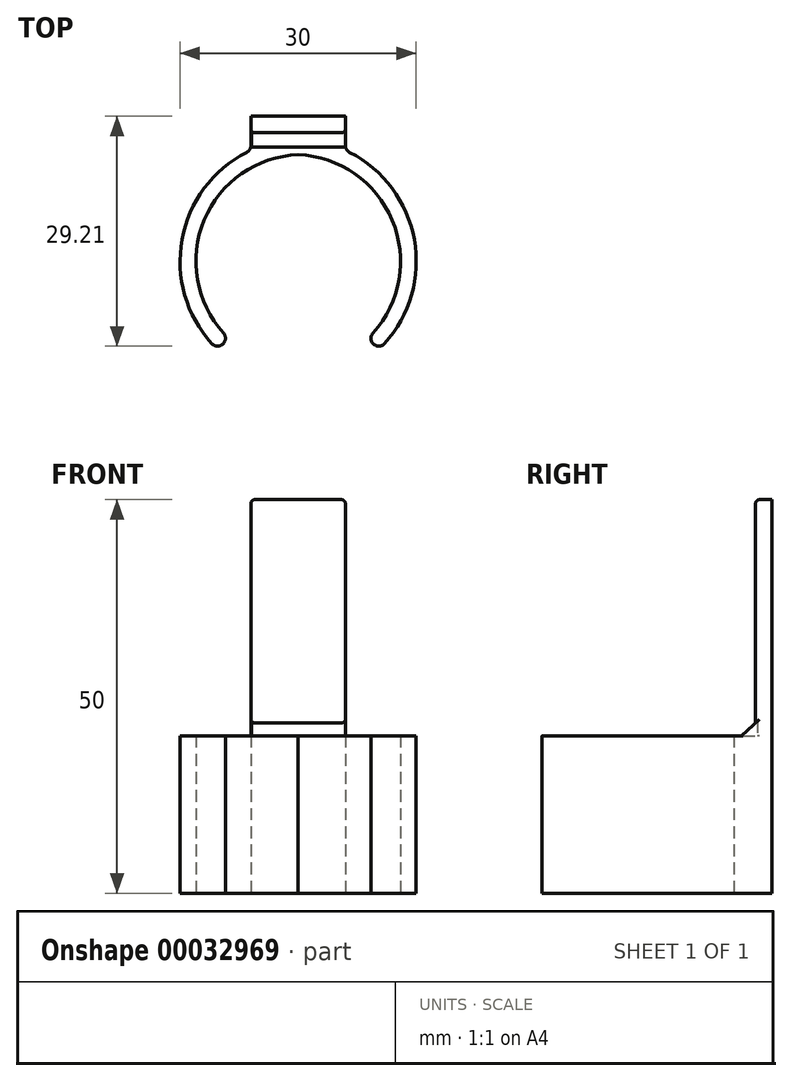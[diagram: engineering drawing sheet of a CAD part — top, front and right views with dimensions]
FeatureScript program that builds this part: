
annotation { "Feature Type Name" : "Feature", "Feature Type Description" : "" }
export const myFeature = defineFeature(function(context is Context, id is Id, definition is map)
    precondition{}
    {
        {
            var Q0;
            Q0=qCreatedBy(makeId("Top.planeOp"),FACE);
            var sketch = newSketch(context, id + "F0", { "sketchPlane" : qUnion([Q0])});
            skCircle(sketch, "E0", {"center": v(0, 0) * mm, "radius": 14.5 * mm, "construction": true});
            skCircle(sketch, "E1", {"center": v(0, 0) * mm, "radius": 12.5 * mm, "construction": true});
            skLineSegment(sketch, "E2", {"start": v(0, 0) * mm, "end": v(10.25, -10.25) * mm, "construction": true});
            skArc(sketch, "E3", {"start": v(9.5, -8.16) * mm, "mid": v(11.95, 6.19) * mm, "end": v(0, 14.5) * mm});
            skArc(sketch, "E4.0", {"start": v(10.98, -9.5) * mm, "mid": v(14.75, 3.74) * mm, "end": v(6.54, 14.8) * mm});
            skLineSegment(sketch, "E5", {"start": v(9.53, -9.53) * mm, "end": v(9.53, -9.53) * mm});
            skPoint(sketch, "E6.visualSharp", {"position": v(8.84, -8.84) * mm});
            skArc(sketch, "E6.filletArc", {"start": v(9.5, -8.16) * mm, "mid": v(9.24, -8.85) * mm, "end": v(9.53, -9.53) * mm});
            skPoint(sketch, "E7.visualSharp", {"position": v(10.25, -10.25) * mm});
            skArc(sketch, "E7.filletArc", {"start": v(9.53, -9.53) * mm, "mid": v(10.27, -9.83) * mm, "end": v(10.98, -9.5) * mm});
            skArc(sketch, "E8.MirrorCS", {"start": v(-10.98, -9.5) * mm, "mid": v(-14.75, 3.74) * mm, "end": v(-6.54, 14.8) * mm});
            skArc(sketch, "E9.MirrorCS", {"start": v(-9.5, -8.16) * mm, "mid": v(-11.95, 6.19) * mm, "end": v(0, 14.5) * mm});
            skArc(sketch, "E10.MirrorCS", {"start": v(-9.5, -8.16) * mm, "mid": v(-9.24, -8.85) * mm, "end": v(-9.53, -9.53) * mm});
            skArc(sketch, "E11.MirrorCS", {"start": v(-9.53, -9.53) * mm, "mid": v(-10.27, -9.83) * mm, "end": v(-10.98, -9.5) * mm});
            skLineSegment(sketch, "E12", {"start": v(6, 15.68) * mm, "end": v(6, 17.28) * mm});
            skLineSegment(sketch, "E13", {"start": v(6, 17.28) * mm, "end": v(0, 17.28) * mm});
            skPoint(sketch, "E14.start.orphan", {"position": v(0, 15.62) * mm});
            skLineSegment(sketch, "E15.MirrorCS", {"start": v(-6, 17.28) * mm, "end": v(0, 17.28) * mm});
            skLineSegment(sketch, "E16.MirrorCS", {"start": v(-6, 15.68) * mm, "end": v(-6, 17.28) * mm});
            skPoint(sketch, "E17.end.orphan", {"position": v(0.08, 16.5) * mm});
            skPoint(sketch, "E17.start.orphan", {"position": v(-0.08, 16.5) * mm});
            skPoint(sketch, "E18.visualSharp", {"position": v(-6, 15.06) * mm});
            skArc(sketch, "E18.filletArc", {"start": v(-6.54, 14.8) * mm, "mid": v(-6.15, 15.16) * mm, "end": v(-6, 15.68) * mm});
            skPoint(sketch, "E19.visualSharp", {"position": v(6, 15.06) * mm});
            skArc(sketch, "E19.filletArc", {"start": v(6, 15.68) * mm, "mid": v(6.15, 15.16) * mm, "end": v(6.54, 14.8) * mm});
            skSolve(sketch);
        }
        {
            var Q0;
            Q0=qSketchRegion(id+"F0",true);
            extrude(context, id + "F1", {"entities" : qUnion([Q0]), "depth" : 20 * mm});
        }
        {
            var Q0;
            Q0=makeQuery(id+"F1.opExtrude","CAP_FACE",FACE,{"disambiguationData":[OSD([sQuery(id+"F0.wireOp",EDGE,"E3"),sQuery(id+"F0.wireOp",EDGE,"E4.0"),sQuery(id+"F0.wireOp",EDGE,"E6.filletArc"),sQuery(id+"F0.wireOp",EDGE,"E7.filletArc"),sQuery(id+"F0.wireOp",EDGE,"E8.MirrorCS"),sQuery(id+"F0.wireOp",EDGE,"E9.MirrorCS"),sQuery(id+"F0.wireOp",EDGE,"E10.MirrorCS"),sQuery(id+"F0.wireOp",EDGE,"E11.MirrorCS"),sQuery(id+"F0.wireOp",EDGE,"E12"),sQuery(id+"F0.wireOp",EDGE,"E13"),sQuery(id+"F0.wireOp",EDGE,"E15.MirrorCS"),sQuery(id+"F0.wireOp",EDGE,"E16.MirrorCS"),sQuery(id+"F0.wireOp",EDGE,"E18.filletArc"),sQuery(id+"F0.wireOp",EDGE,"E19.filletArc")])],"isStart":true});
            var sketch = newSketch(context, id + "F2", { "sketchPlane" : qUnion([Q0])});
            skLineSegment(sketch, "E20.bottom", {"start": v(6, -17.28) * mm, "end": v(-6, -17.28) * mm});
            skLineSegment(sketch, "E20.top", {"start": v(6, -19.38) * mm, "end": v(-6, -19.38) * mm});
            skLineSegment(sketch, "E20.left", {"start": v(6, -17.28) * mm, "end": v(6, -19.38) * mm});
            skLineSegment(sketch, "E20.right", {"start": v(-6, -17.28) * mm, "end": v(-6, -19.38) * mm});
            skSolve(sketch);
        }
        {
            var Q0;
            Q0=qSketchRegion(id+"F2",true);
            extrude(context, id + "F3", {"entities" : qUnion([Q0]), "oppositeDirection" : true, "depth" : 50 * mm});
        }
        {
            var Q0;
            Q0=makeQuery(id+"F3.opExtrude","SWEPT_FACE",FACE,{"disambiguationData":[OSD([sQuery(id+"F2.wireOp",EDGE,"E20.left")])]});
            var sketch = newSketch(context, id + "F4", { "sketchPlane" : qUnion([Q0])});
            skLineSegment(sketch, "E21", {"start": v(14.9, 19.5) * mm, "end": v(17.28, 19.5) * mm});
            skLineSegment(sketch, "E22", {"start": v(17.28, 19.5) * mm, "end": v(17.28, 21.65) * mm});
            skLineSegment(sketch, "E23", {"start": v(17.28, 21.65) * mm, "end": v(14.9, 19.5) * mm});
            skSolve(sketch);
        }
        {
            var Q0;
            Q0=qSketchRegion(id+"F4",true);
            extrude(context, id + "F5", {"entities" : qUnion([Q0]), "operationType" : NewBodyOperationType.ADD, "oppositeDirection" : true, "depth" : 11.93 * mm});
        }
        {
            var Q0;
            {var subQ0=sQuery(id+"F2.wireOp",EDGE,"E20.bottom");var subQ1=sQuery(id+"F2.wireOp",EDGE,"E20.left");var subQ2=sQuery(id+"F4.wireOp",EDGE,"E23");Q0=makeQuery(id+"F5.boolean.opBoolean","SPLIT",EDGE,{"disambiguationData":[TD([makeQuery(id+"F5.opExtrude","SWEPT_FACE",FACE,{"disambiguationData":[OSD([subQ2])]})])],"derivedFrom":makeQuery(id+"F3.opExtrude","SWEPT_EDGE",EDGE,{"disambiguationData":[OSD([sQuery(id+"F0.wireOp",EDGE,"E12"),subQ0,subQ1])]})});}
            var Q1;
            Q1=makeQuery(id+"F3.opExtrude","SWEPT_EDGE",EDGE,{"disambiguationData":[OSD([sQuery(id+"F0.wireOp",EDGE,"E16.MirrorCS"),sQuery(id+"F2.wireOp",EDGE,"E20.bottom"),sQuery(id+"F2.wireOp",EDGE,"E20.right")])]});
            fillet(context, id + "F6", {"entities" : qUnion([Q0, Q1]), "radius" : .5 * mm, "tangentPropagation" : true, "allowEdgeOverflow" : false});
        }
        {
            var Q0;
            Q0=makeQuery(id+"F3.opExtrude","CAP_EDGE",EDGE,{"disambiguationData":[OSD([sQuery(id+"F2.wireOp",EDGE,"E20.bottom")])],"isStart":false});
            fillet(context, id + "F7", {"entities" : qUnion([Q0]), "radius" : .5 * mm, "tangentPropagation" : true, "allowEdgeOverflow" : false});
        }
    });
